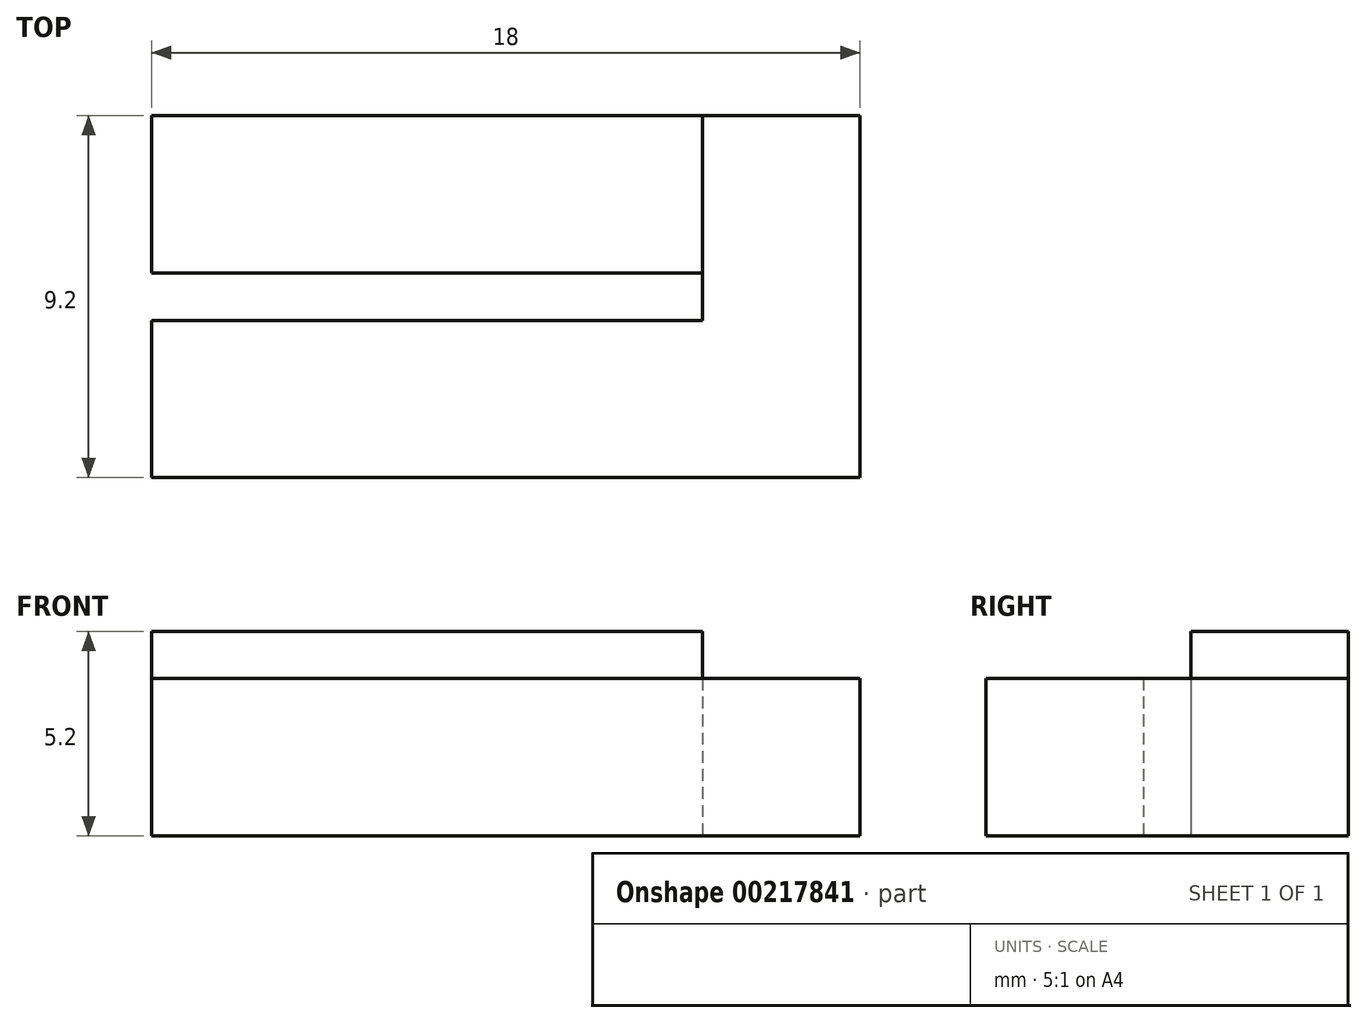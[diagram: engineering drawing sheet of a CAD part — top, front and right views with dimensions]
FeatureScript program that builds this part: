
annotation { "Feature Type Name" : "Feature", "Feature Type Description" : "" }
export const myFeature = defineFeature(function(context is Context, id is Id, definition is map)
    precondition{}
    {
        {
            var Q0;
            Q0=qCreatedBy(makeId("Top.planeOp"),FACE);
            var sketch = newSketch(context, id + "F0", { "sketchPlane" : qUnion([Q0])});
            skLineSegment(sketch, "E0", {"start": v(0, 0) * mm, "end": v(-14, 0) * mm});
            skLineSegment(sketch, "E1", {"start": v(-14, 0) * mm, "end": v(-14, -4) * mm});
            skLineSegment(sketch, "E2", {"start": v(-14, -4) * mm, "end": v(4, -4) * mm});
            skLineSegment(sketch, "E3", {"start": v(4, -4) * mm, "end": v(4, 5.2) * mm});
            skLineSegment(sketch, "E4", {"start": v(4, 5.2) * mm, "end": v(-14, 5.2) * mm});
            skLineSegment(sketch, "E5", {"start": v(-14, 5.2) * mm, "end": v(-14, 1.2) * mm});
            skLineSegment(sketch, "E6", {"start": v(-14, 1.2) * mm, "end": v(0, 1.2) * mm});
            skLineSegment(sketch, "E7", {"start": v(0, 1.2) * mm, "end": v(0, 0) * mm});
            skLineSegment(sketch, "E8", {"start": v(0, 1.2) * mm, "end": v(0, 5.2) * mm});
            skPoint(sketch, "E8.endSnap0", {"position": v(-5, 5.2) * mm});
            skSolve(sketch);
        }
        {
            var Q0;
            {var subQ0=sQuery(id+"F0.wireOp",EDGE,"E5");Q0=makeQuery(id+"F0.imprint","IMPRINT",FACE,{"disambiguationData":[TD([[makeQuery(id+"F0.imprint","IMPRINT",EDGE,{"derivedFrom":subQ0}),1.0]])]});}
            extrude(context, id + "F1", {"entities" : qUnion([Q0]), "depth" : 5.2 * mm});
        }
        {
            var Q0;
            Q0=makeQuery(id+"F0.imprint","IMPRINT",FACE,{"disambiguationData":[TD([[makeQuery(id+"F0.imprint","IMPRINT",EDGE,{"derivedFrom":sQuery(id+"F0.wireOp",EDGE,"E0")}),1.0]])]});
            extrude(context, id + "F2", {"entities" : qUnion([Q0]), "operationType" : NewBodyOperationType.ADD, "depth" : 4 * mm});
        }
    });
